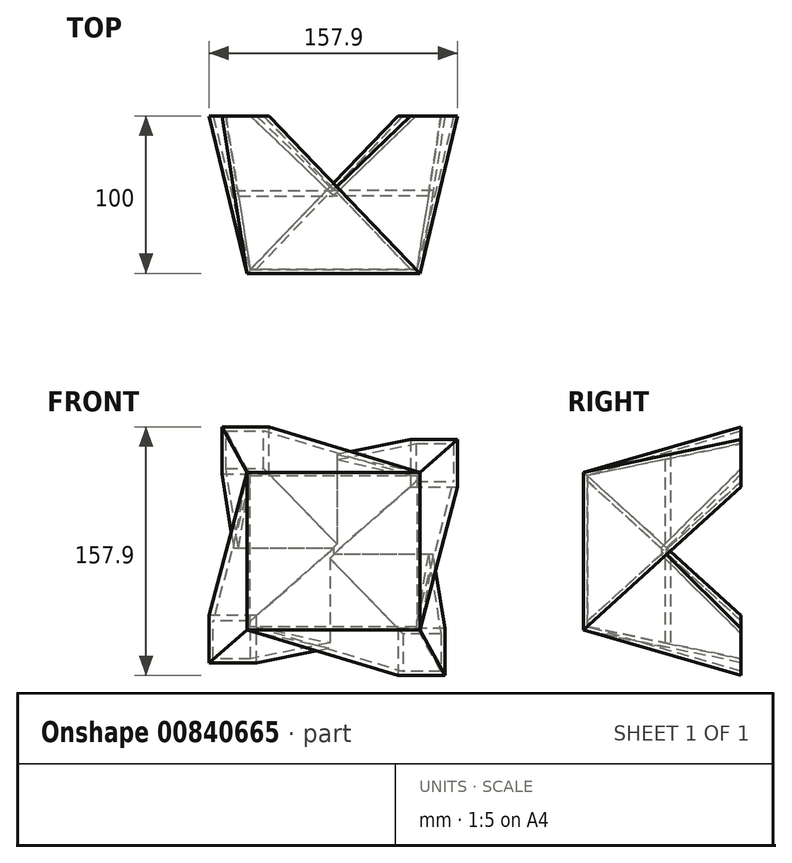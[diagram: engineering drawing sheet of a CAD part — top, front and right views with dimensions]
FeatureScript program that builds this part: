
annotation { "Feature Type Name" : "Feature", "Feature Type Description" : "" }
export const myFeature = defineFeature(function(context is Context, id is Id, definition is map)
    precondition{}
    {
        {
            var Q0;
            Q0=qCreatedBy(makeId("Front.planeOp"),FACE);
            var sketch = newSketch(context, id + "F0", { "sketchPlane" : qUnion([Q0])});
            skLineSegment(sketch, "E0.bottom", {"start": v(-55, 50) * mm, "end": v(55, 50) * mm});
            skLineSegment(sketch, "E0.top", {"start": v(-55, -50) * mm, "end": v(55, -50) * mm});
            skLineSegment(sketch, "E0.left", {"start": v(-55, 50) * mm, "end": v(-55, -50) * mm});
            skLineSegment(sketch, "E0.right", {"start": v(55, 50) * mm, "end": v(55, -50) * mm});
            skPoint(sketch, "E0.middle", {"position": v(0, 0) * mm});
            skSolve(sketch);
        }
        {
            var Q0;
            Q0=qCreatedBy(makeId("Front.planeOp"),FACE);
            cPlane(context, id + "F1", {"entities" : qUnion([Q0]), "cplaneType" : CPlaneType.OFFSET, "offset" : 100 * mm, "oppositeDirection" : true, "width" : 150 * mm, "height" : 150 * mm});
        }
        {
            var Q0;
            Q0=qCreatedBy(id+"F1.planeOp",FACE);
            var sketch = newSketch(context, id + "F2", { "sketchPlane" : qUnion([Q0])});
            skLineSegment(sketch, "E1.bottom", {"start": v(48.95, 70.87) * mm, "end": v(78.95, 70.87) * mm});
            skLineSegment(sketch, "E1.top", {"start": v(48.95, 40.87) * mm, "end": v(78.95, 40.87) * mm});
            skLineSegment(sketch, "E1.left", {"start": v(48.95, 70.87) * mm, "end": v(48.95, 40.87) * mm});
            skLineSegment(sketch, "E1.right", {"start": v(78.95, 70.87) * mm, "end": v(78.95, 40.87) * mm});
            skPoint(sketch, "E1.middle", {"position": v(63.95, 55.87) * mm});
            skLineSegment(sketch, "E2.1.0", {"start": v(-70.87, 48.95) * mm, "end": v(-70.87, 78.95) * mm});
            skLineSegment(sketch, "E2.1.1", {"start": v(-70.87, 48.95) * mm, "end": v(-40.87, 48.95) * mm});
            skLineSegment(sketch, "E2.1.2", {"start": v(-40.87, 48.95) * mm, "end": v(-40.87, 78.95) * mm});
            skLineSegment(sketch, "E2.1.3", {"start": v(-70.87, 78.95) * mm, "end": v(-40.87, 78.95) * mm});
            skLineSegment(sketch, "E2.2.0", {"start": v(-48.95, -70.87) * mm, "end": v(-78.95, -70.87) * mm});
            skLineSegment(sketch, "E2.2.1", {"start": v(-48.95, -70.87) * mm, "end": v(-48.95, -40.87) * mm});
            skLineSegment(sketch, "E2.2.2", {"start": v(-48.95, -40.87) * mm, "end": v(-78.95, -40.87) * mm});
            skLineSegment(sketch, "E2.2.3", {"start": v(-78.95, -70.87) * mm, "end": v(-78.95, -40.87) * mm});
            skLineSegment(sketch, "E2.3.0", {"start": v(70.87, -48.95) * mm, "end": v(70.87, -78.95) * mm});
            skLineSegment(sketch, "E2.3.1", {"start": v(70.87, -48.95) * mm, "end": v(40.87, -48.95) * mm});
            skLineSegment(sketch, "E2.3.2", {"start": v(40.87, -48.95) * mm, "end": v(40.87, -78.95) * mm});
            skLineSegment(sketch, "E2.3.3", {"start": v(70.87, -78.95) * mm, "end": v(40.87, -78.95) * mm});
            skPoint(sketch, "E2.center", {"position": v(0, 0) * mm});
            skSolve(sketch);
        }
        {
            var Q0;
            Q0=makeQuery(id+"F2.imprint","IMPRINT",FACE,{"disambiguationData":[TD([[makeQuery(id+"F2.imprint","IMPRINT",EDGE,{"derivedFrom":sQuery(id+"F2.wireOp",EDGE,"E2.3.0")}),-1.0]])]});
            var Q1;
            Q1=makeQuery(id+"F0.imprint","IMPRINT",FACE,{"disambiguationData":[TD([[makeQuery(id+"F0.imprint","IMPRINT",EDGE,{"derivedFrom":sQuery(id+"F0.wireOp",EDGE,"E0.bottom")}),-1.0]])]});
            loft(context, id + "F3", {"sheetProfilesArray" : [{ "sheetProfileEntities" : qUnion([Q0]) }, { "sheetProfileEntities" : qUnion([Q1]) }]});
        }
        {
            var Q1;
            Q1=makeQuery(id+"F2.imprint","IMPRINT",FACE,{"disambiguationData":[TD([[makeQuery(id+"F2.imprint","IMPRINT",EDGE,{"derivedFrom":sQuery(id+"F2.wireOp",EDGE,"E1.bottom")}),-1.0]])]});
            var Q2;
            Q2=makeQuery(id+"F3.opLoft","CAP_FACE",FACE,{"disambiguationData":[OSD([makeQuery(id+"F0.imprint","IMPRINT",FACE,{"disambiguationData":[TD([[makeQuery(id+"F0.imprint","IMPRINT",EDGE,{"derivedFrom":sQuery(id+"F0.wireOp",EDGE,"E0.bottom")}),-1.0]])]})])],"isStart":true});
            loft(context, id + "F4", {"operationType" : NewBodyOperationType.ADD, "sheetProfilesArray" : [{ "sheetProfileEntities" : qUnion([Q1]) }, { "sheetProfileEntities" : qUnion([Q2]) }]});
        }
        {
            var Q1;
            Q1=makeQuery(id+"F2.imprint","IMPRINT",FACE,{"disambiguationData":[TD([[makeQuery(id+"F2.imprint","IMPRINT",EDGE,{"derivedFrom":sQuery(id+"F2.wireOp",EDGE,"E2.1.0")}),-1.0]])]});
            var Q2;
            Q2=makeQuery(id+"F3.opLoft","CAP_FACE",FACE,{"disambiguationData":[OSD([makeQuery(id+"F0.imprint","IMPRINT",FACE,{"disambiguationData":[TD([[makeQuery(id+"F0.imprint","IMPRINT",EDGE,{"derivedFrom":sQuery(id+"F0.wireOp",EDGE,"E0.bottom")}),-1.0]])]})])],"isStart":true});
            loft(context, id + "F5", {"operationType" : NewBodyOperationType.ADD, "sheetProfilesArray" : [{ "sheetProfileEntities" : qUnion([Q1]) }, { "sheetProfileEntities" : qUnion([Q2]) }]});
        }
        {
            var Q1;
            Q1=makeQuery(id+"F2.imprint","IMPRINT",FACE,{"disambiguationData":[TD([[makeQuery(id+"F2.imprint","IMPRINT",EDGE,{"derivedFrom":sQuery(id+"F2.wireOp",EDGE,"E2.2.0")}),-1.0]])]});
            var Q2;
            Q2=makeQuery(id+"F3.opLoft","CAP_FACE",FACE,{"disambiguationData":[OSD([makeQuery(id+"F0.imprint","IMPRINT",FACE,{"disambiguationData":[TD([[makeQuery(id+"F0.imprint","IMPRINT",EDGE,{"derivedFrom":sQuery(id+"F0.wireOp",EDGE,"E0.bottom")}),-1.0]])]})])],"isStart":true});
            loft(context, id + "F6", {"operationType" : NewBodyOperationType.ADD, "sheetProfilesArray" : [{ "sheetProfileEntities" : qUnion([Q1]) }, { "sheetProfileEntities" : qUnion([Q2]) }]});
        }
        {
            var Q0;
            Q0=makeQuery(id+"F5.opLoft","CAP_FACE",FACE,{"disambiguationData":[OSD([makeQuery(id+"F2.imprint","IMPRINT",FACE,{"disambiguationData":[TD([[makeQuery(id+"F2.imprint","IMPRINT",EDGE,{"derivedFrom":sQuery(id+"F2.wireOp",EDGE,"E2.1.0")}),-1.0]])]})])],"isStart":true});
            var Q1;
            Q1=makeQuery(id+"F4.opLoft","CAP_FACE",FACE,{"disambiguationData":[OSD([makeQuery(id+"F2.imprint","IMPRINT",FACE,{"disambiguationData":[TD([[makeQuery(id+"F2.imprint","IMPRINT",EDGE,{"derivedFrom":sQuery(id+"F2.wireOp",EDGE,"E1.bottom")}),-1.0]])]})])],"isStart":true});
            var Q2;
            Q2=makeQuery(id+"F3.opLoft","CAP_FACE",FACE,{"disambiguationData":[OSD([makeQuery(id+"F2.imprint","IMPRINT",FACE,{"disambiguationData":[TD([[makeQuery(id+"F2.imprint","IMPRINT",EDGE,{"derivedFrom":sQuery(id+"F2.wireOp",EDGE,"E2.3.0")}),-1.0]])]})])],"isStart":true});
            var Q3;
            Q3=makeQuery(id+"F6.opLoft","CAP_FACE",FACE,{"disambiguationData":[OSD([makeQuery(id+"F2.imprint","IMPRINT",FACE,{"disambiguationData":[TD([[makeQuery(id+"F2.imprint","IMPRINT",EDGE,{"derivedFrom":sQuery(id+"F2.wireOp",EDGE,"E2.2.0")}),-1.0]])]})])],"isStart":true});
            shell(context, id + "F7", {"entities" : qUnion([Q0, Q1, Q2, Q3]), "thickness" : 2.5 * mm});
        }
    });
